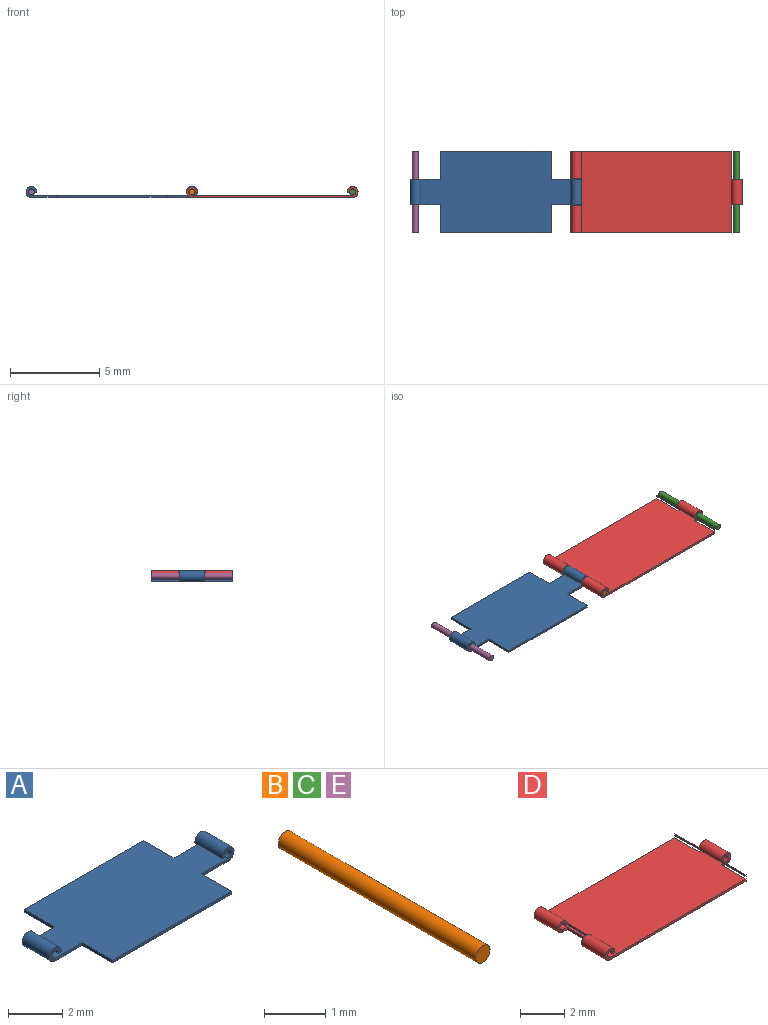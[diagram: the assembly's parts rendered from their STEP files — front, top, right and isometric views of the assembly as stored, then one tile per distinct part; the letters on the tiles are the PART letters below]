
ASSEMBLY  parts=5 mates=4
PART A: 18 faces, bbox 9.6x4.6x0.6 mm
  f0: plane 9.02x4.58mm, normal (0,0,-1), area 32.5mm2, adj f1,f5,f6,f9,f10,f11,f12,f13
  f1: plane 6.22x0.13mm, normal (0,-1,0), area 0.8mm2, adj f0,f2,f10,f14
  f2: plane 9.02x4.58mm, normal (0,0,1), area 32.5mm2, adj f1,f3,f8,f9,f10,f11,f12,f13
  f3: cylinder r=0.18mm len=1.43mm, axis (0,1,0), area 1.3mm2, adj f2,f4,f15,f16
  f4: plane 1.43x0.13mm, normal (0,0,-1), area 0.2mm2, adj f3,f5,f15,f16
  f5: cylinder r=0.3mm len=1.43mm, axis (0,1,0), area 2.1mm2, adj f0,f4,f15,f16
  f6: cylinder r=0.3mm len=1.43mm, axis (0,1,0), area 2.1mm2, adj f0,f7,f11,f12
  f7: plane 1.43x0.13mm, normal (0,0,-1), area 0.2mm2, adj f6,f8,f11,f12
  f8: cylinder r=0.18mm len=1.43mm, axis (0,1,0), area 1.3mm2, adj f2,f7,f11,f12
  f9: plane 6.22x0.13mm, normal (0,1,0), area 0.8mm2, adj f0,f2,f13,f17
  f10: plane 1.58x0.13mm, normal (-1,0,0), area 0.2mm2, adj f0,f1,f2,f11
  f11: plane 1.7x0.61mm, normal (0,-1,0), area 0.3mm2, adj f0,f2,f6,f7,f8,f10
  f12: plane 1.7x0.61mm, normal (0,1,0), area 0.3mm2, adj f0,f2,f6,f7,f8,f13
  f13: plane 1.58x0.13mm, normal (-1,0,0), area 0.2mm2, adj f0,f2,f9,f12
  f14: plane 1.58x0.13mm, normal (1,0,0), area 0.2mm2, adj f0,f1,f2,f15
  f15: plane 1.7x0.61mm, normal (0,-1,0), area 0.3mm2, adj f0,f2,f3,f4,f5,f14
  f16: plane 1.7x0.61mm, normal (0,1,0), area 0.3mm2, adj f0,f2,f3,f4,f5,f17
  f17: plane 1.58x0.13mm, normal (1,0,0), area 0.2mm2, adj f0,f2,f9,f16
PART B: 3 faces, bbox 0.3x4.6x0.3 mm
  f0: plane 0.33x0.33mm, normal (0,-1,0), area 0.1mm2, adj f2
  f1: plane 0.33x0.33mm, normal (0,1,0), area 0.1mm2, adj f2
  f2: cylinder r=0.17mm len=4.58mm, axis (0,1,0), area 4.8mm2, adj f0,f1
PART C: same geometry as B
PART D: 22 faces, bbox 9.6x4.6x0.6 mm
  f0: plane 9.02x0.61mm, normal (0,1,0), area 1.3mm2, adj f1,f4,f8,f9,f10,f12
  f1: plane 9.02x4.58mm, normal (0,0,1), area 39.9mm2, adj f0,f2,f7,f8,f11,f12,f13,f15
  f2: cylinder r=0.18mm len=1.53mm, axis (0,-1,0), area 1.4mm2, adj f1,f3,f11,f19
  f3: plane 1.53x0.13mm, normal (0,0,-1), area 0.2mm2, adj f2,f10,f11,f19
  f4: plane 9.02x4.58mm, normal (0,0,-1), area 39.9mm2, adj f0,f5,f10,f11,f12,f13,f15,f16
  f5: cylinder r=0.3mm len=4.58mm, axis (0,-1,0), area 2.4mm2, adj f4,f6,f13,f14,f15,f17
  f6: plane 1.43x0.13mm, normal (0,0,-1), area 0.2mm2, adj f5,f7,f13,f15
  f7: cylinder r=0.18mm len=1.43mm, axis (0,-1,0), area 1.3mm2, adj f1,f6,f13,f15
  f8: cylinder r=0.18mm len=1.53mm, axis (0,-1,0), area 1.4mm2, adj f0,f1,f9,f18
  f9: plane 1.53x0.13mm, normal (0,0,-1), area 0.2mm2, adj f0,f8,f10,f18
  f10: cylinder r=0.3mm len=4.58mm, axis (0,-1,0), area 4.7mm2, adj f0,f3,f4,f9,f11,f18,f19,f21
  f11: plane 9.02x0.61mm, normal (0,-1,0), area 1.3mm2, adj f1,f2,f3,f4,f10,f16
  f12: plane 1.58x0.13mm, normal (1,0,0), area 0.2mm2, adj f0,f1,f4,f13
  f13: plane 0.61x0.61mm, normal (0,1,0), area 0.2mm2, adj f1,f4,f5,f6,f7,f12,f14
  f14: plane 1.59x0.11mm, normal (1,0,0), area 0.2mm2, adj f5,f13
  f15: plane 0.61x0.61mm, normal (0,-1,0), area 0.2mm2, adj f1,f4,f5,f6,f7,f16,f17
  f16: plane 1.58x0.13mm, normal (1,0,0), area 0.2mm2, adj f1,f4,f11,f15
  f17: plane 1.59x0.11mm, normal (1,0,0), area 0.2mm2, adj f5,f15
  f18: plane 0.61x0.61mm, normal (0,-1,0), area 0.2mm2, adj f1,f4,f8,f9,f10,f20,f21
  f19: plane 0.61x0.61mm, normal (0,1,0), area 0.2mm2, adj f1,f2,f3,f4,f10,f20,f21
  f20: plane 1.53x0.13mm, normal (-1,0,0), area 0.2mm2, adj f1,f4,f18,f19
  f21: plane 1.53x0.1mm, normal (-1,0,0), area 0.2mm2, adj f10,f18,f19
PART E: same geometry as B
PLACE A t=(-349.12,-3.44,-40.57)mm
PLACE B t=(-340.11,-3.44,-40.57)mm
PLACE C t=(-331.09,-3.44,-40.57)mm
PLACE D t=(-349.12,-3.44,-40.57)mm
PLACE E t=(-349.12,-3.44,-40.57)mm
MATE revolute C.f2 <-> D.f5  axis (0,1,0) through (-28.96,-3.44,-18.83)mm
MATE revolute E.f2 <-> A.f6  axis (0,1,0) through (-46.99,-3.44,-18.83)mm
MATE revolute D.f2 <-> B.f2  axis (0,-1,0) through (-37.97,-5.73,-18.83)mm
MATE revolute A.f3 <-> B.f2  axis (0,1,0) through (-37.97,-3.44,-18.83)mm
